# Revit family: СИБ
name_source: partatom
category: Электрические приборы
units: mm (PartAtom-declared; Revit-internal decimal feet)

## family parameters
Всегда вертикально = Нет
Заголовок OmniClass = Electric Power and Lighting
Номер OmniClass = 23.80.00.00
Общий = Нет
Основа = Стена
При загрузке вырезать с полостями = Нет
Размер круглого соединителя = Использовать диаметр
Сохранять ориентацию аннотаций = Нет
Тип детали = Нормальный
Точка расчета площади = Нет

## types (28) — shared parameters
ADSK_Единица измерения = шт.
ADSK_Завод-изготовитель = Chronos Meter
ADSK_Количество = 1
Высота размещения = 1498 мм
Высота_крепление = 43 мм
Каналы = 4
Сайт производителя = https://chronosmeter.com
Ширина с креплением = 145 мм

## per-type parameters (varying)
| type | ADSK_Код изделия | ADSK_Марка | ADSK_Масса | ADSK_Наименование | SMA разъем | Sim-карта в комплекте | Антенна | Высота | Гермовводы | Глубина, мм | Интерфейс | Крепление на стену | Питание | Степень_защиты_IP | Температурный режим | Уплотнители IP20 | Ширина, мм |
| SET.SIB.LR.4.20.0.0.0.0 | C199-1104 | SET.SIB.LR.4.20.0.0.0.0 | 0.15 | Счетчик импульсов беспроводной 4канальный LoRaWAN | Нет | Нет | внутренняя | 48 мм | Нет | 38 мм | LoRaWAN | Нет | внутреннее | 20 | 0 +55ºС | Да | 99 мм |
| SET.SIB.LR.4.20.S.0.0.0 | C199-1105 | SET.SIB.LR.4.20.S.0.0.0 | 0.15 | Счетчик импульсов беспроводной 4канальный LoRaWAN | Да | Нет | внешняя | 48 мм | Нет | 38 мм | LoRaWAN | Нет | внутреннее | 20 | 0 +55ºС | Да | 99 мм |
| SET.SIB.LR.4.65.0.0.0.0 | C199-1136 | SET.SIB.LR.4.65.0.0.0.0 | 0.2 | Счетчик импульсов беспроводной 4канальный LoRaWAN | Нет | Нет | внутренняя | 64 мм | Да | 40 мм | LoRaWAN | Да | внутреннее | 65 | 0 +55ºС | Нет | 115 мм |
| SET.SIB.LR.4.65.S.0.0.0 | C199-1137 | SET.SIB.LR.4.65.0.0.0.0 | 0.2 | Счетчик импульсов беспроводной 4канальный LoRaWAN | Да | Нет | внешняя | 64 мм | Да | 40 мм | LoRaWAN | Да | внутреннее | 65 | 0 +55ºС | Нет | 115 мм |
| SET.SIB.LR.4.68.A.0.0.0 | C199-1156 | SET.SIB.LR.4.68.A.0.0.0 | 0.2 | Счетчик импульсов беспроводной 4канальный LoRaWAN | Нет | Нет | внешняя | 64 мм | Да | 40 мм | LoRaWAN | Да | внутреннее | 68 | 0 +55ºС | Нет | 115 мм |
| SET.SIB.LR.4.68.A.0.1.0 | C199-1157 | SET.SIB.LR.4.68.A.0.1.0 | 0.2 | Счетчик импульсов беспроводной 4канальный LoRaWAN | Нет | Нет | внешняя | 64 мм | Да | 40 мм | LoRaWAN | Да | внутреннее | 68 | -40 +55ºС | Нет | 115 мм |
| SET.SIB.GSM.4.65.S.0.0.0 | C199-1219 | SET.SIB.GSM.4.65.S.0.0.0 | 0.2 | Счетчик импульсов беспроводной 4канальный GSM | Да | Нет | внешняя | 64 мм | Да | 40 мм | GSM | Да | внутреннее | 65 | 0 +55ºС | Нет | 115 мм |
| SET.SIB.GSM.4.65.S.1.1.0 | C199-1225 | SET.SIB.GSM.4.65.S.1.1.0 | 0.2 | Счетчик импульсов беспроводной 4канальный GSM | Да | Нет | внешняя | 64 мм | Да | 40 мм | GSM | Да | внешнее | 65 | -40 +55ºС | Нет | 115 мм |
| SET.SIB.GSM.4.68.A.0.0.0 | C199-1243 | SET.SIB.GSM.4.68.A.0.0.0 | 0.2 | Счетчик импульсов беспроводной 4канальный GSM | Нет | Нет | внешняя | 64 мм | Да | 40 мм | GSM | Да | внутреннее | 68 | 0 +55ºС | Нет | 115 мм |
| SET.SIB.NB.4.65.S.0.0.0 | C199-1319 | SET.SIB.GSM.4.65.S.0.0.0 | 0.2 | Счетчик импульсов беспроводной 4канальный NB-IoT | Да | Нет | внешняя | 64 мм | Да | 40 мм | NB-IoT | Да | внутреннее | 65 | 0 +55ºС | Нет | 115 мм |
| SET.SIB.NB.4.65.S.1.1.0 | C199-1325 | SET.SIB.GSM.4.65.S.1.1.0 | 0.2 | Счетчик импульсов беспроводной 4канальный NB-IoT | Да | Нет | внешняя | 64 мм | Да | 40 мм | NB-IoT | Да | внешнее | 65 | -40 +55ºС | Нет | 115 мм |
| SET.SIB.NB.4.68.A.0.0.0 | C199-1343 | SET.SIB.NB.4.68.A.0.0.0 | 0.2 | Счетчик импульсов беспроводной 4канальный NB-IoT | Нет | Нет | внешняя | 64 мм | Да | 40 мм | GSM | Да | внутреннее | 68 | 0 +55ºС | Нет | 115 мм |
| SET.SIB.NB.4.65.S.0.0.SIM.C | C199-1348 | SET.SIB.NB.4.65.S.0.0.SIM.C | 0.2 | Счетчик импульсов беспроводной 4канальный NB-IoT | Да | Да | внешняя | 64 мм | Да | 40 мм | NB-IoT | Да | внутреннее | 65 | 0 +55ºС | Нет | 115 мм |
| SET.SIB.NB.4.68.A.0.0.SIM.C | C199-1351 | SET.SIB.NB.4.68.A.0.0.SIM.C | 0.2 | Счетчик импульсов беспроводной 4канальный NB-IoT | Нет | Да | внешняя | 64 мм | Да | 40 мм | GSM | Да | внутреннее | 68 | 0 +55ºС | Нет | 115 мм |
| SET.SIB.RF.4.20.0.0.0.0 | C199-1000 | SET.SIB.RF.4.20.0.0.0.0 | 0.15 | Счетчик импульсов беспроводной 4канальный wM-Bus | Нет | Нет | внутренняя | 48 мм | Нет | 38 мм | RF-433 | Нет | внутреннее | 20 | 0 +55ºС | Да | 99 мм |
| SET.SIB.RF.4.20.S.0.0.0 | C199-1001 | SET.SIB.RF.4.20.S.0.0.0 | 0.15 | Счетчик импульсов беспроводной 4канальный wM-Bus | Да | Нет | внешняя | 48 мм | Нет | 38 мм | RF-433 | Нет | внутреннее | 20 | 0 +55ºС | Да | 99 мм |
| SET.SIB.RF.4.65.0.0.0.0 | C199-1006 | SET.SIB.RF.4.65.0.0.0.0 | 0.2 | Счетчик импульсов беспроводной 4канальный wM-Bus | Нет | Нет | внутренняя | 64 мм | Да | 40 мм | RF-433 | Да | внутреннее | 65 | 0 +55ºС | Нет | 115 мм |
| SET.SIB.RF.4.65.S.0.0.0 | C199-1007 | SET.SIB.RF.4.65.S.0.0.0 | 0.2 | Счетчик импульсов беспроводной 4канальный wM-Bus | Да | Нет | внешняя | 64 мм | Да | 40 мм | RF-433 | Да | внутреннее | 65 | 0 +55ºС | Нет | 115 мм |
| SET.SIB.RF.4.65.0.0.1.0 | C199-1008 | SET.SIB.RF.4.65.0.0.1.0 | 0.2 | Счетчик импульсов беспроводной 4канальный wM-Bus | Нет | Нет | внутренняя | 64 мм | Да | 40 мм | RF-433 | Да | внутреннее | 65 | -40 +55ºС | Нет | 115 мм |
| SET.SIB.RF.4.65.S.0.1.0 | C199-1009 | SET.SIB.RF.4.65.S.0.1.0 | 0.2 | Счетчик импульсов беспроводной 4канальный wM-Bus | Да | Нет | внешняя | 64 мм | Да | 40 мм | RF-433 | Да | внутреннее | 65 | -40 +55ºС | Нет | 115 мм |
| SET.SIB.RF.4.68.A.0.0.0 | C199-1010 | SET.SIB.RF.4.68.A.0.0.0 | 0.2 | Счетчик импульсов беспроводной 4канальный wM-Bus | Нет | Нет | внешняя | 64 мм | Да | 40 мм | RF-433 | Да | внутреннее | 68 | 0 +55ºС | Нет | 115 мм |
| SET.SIB.RF.4.68.A.0.1.0 | C199-1011 | SET.SIB.RF.4.68.A.0.1.0 | 0.2 | Счетчик импульсов беспроводной 4канальный wM-Bus | Нет | Нет | внешняя | 64 мм | Да | 40 мм | RF-433 | Да | внутреннее | 68 | -40 +55ºС | Нет | 115 мм |
| SET.SIB.LR.4.65.0.0.1.0 | C199-1138 | SET.SIB.LR.4.65.0.0.1.0 | 0.2 | Счетчик импульсов беспроводной 4канальный LoRaWAN | Нет | Нет | внутренняя | 64 мм | Да | 40 мм | LoRaWAN | Да | внутреннее | 65 | -40 +55ºС | Нет | 115 мм |
| SET.SIB.LR.4.65.S.0.1.0 | C199-1139 | SET.SIB.LR.4.65.S.0.1.0 | 0.2 | Счетчик импульсов беспроводной 4канальный LoRaWAN | Да | Нет | внешняя | 64 мм | Да | 40 мм | LoRaWAN | Да | внутреннее | 65 | -40 +55ºС | Нет | 115 мм |
| SET.SIB.GSM.4.65.S.0.1.0 | C199-1221 | SET.SIB.GSM.4.65.S.0.1.0 | 0.2 | Счетчик импульсов беспроводной 4канальный GSM | Да | Нет | внешняя | 64 мм | Да | 40 мм | GSM | Да | внутреннее | 65 | -40 +55ºС | Нет | 115 мм |
| SET.SIB.GSM.4.68.A.0.1.0 | C199-1245 | SET.SIB.GSM.4.68.A.0.1.0 | 0.2 | Счетчик импульсов беспроводной 4канальный GSM | Нет | Нет | внешняя | 64 мм | Да | 40 мм | GSM | Да | внутреннее | 68 | -40 +55ºС | Нет | 115 мм |
| SET.SIB.NB.4.65.S.0.1.0 | C199-1321 | SET.SIB.NB.4.65.S.0.1.0 | 0.2 | Счетчик импульсов беспроводной 4канальный NB-IoT | Да | Нет | внешняя | 64 мм | Да | 40 мм | NB-IoT | Да | внутреннее | 65 | -40 +55ºС | Нет | 115 мм |
| SET.SIB.NB.4.68.A.0.1.0 | C199-1345 | SET.SIB.NB.4.68.A.0.1.0 | 0.2 | Счетчик импульсов беспроводной 4канальный NB-IoT | Нет | Нет | внешняя | 64 мм | Да | 40 мм | GSM | Да | внутреннее | 68 | -40 +55ºС | Нет | 115 мм |
